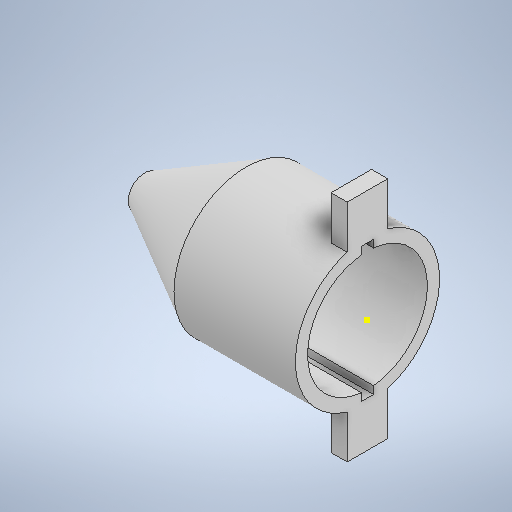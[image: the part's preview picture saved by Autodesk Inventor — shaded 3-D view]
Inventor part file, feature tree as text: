
AUTODESK INVENTOR PART (.ipt)
format: ipt  version: 2025.2 (Build 292293000, 293)  size: 317,952 bytes
history: native  units: in
note: dims shown in document units (in); Inventor stores cm internally (conversion verified against a paired STEP export)
features: sketch x19, extrude x10, revolve x1
ambient origin geometry x8: Origin, YZ Plane, XZ Plane, XY Plane, X Axis, Y Axis, Z Axis, Center Point
bodies: Solid1 (feature_tree)
feature tree (30):
  revolve  "Revolution1"  Angle=90.0deg
  sketch  "Sketch2"  dims[d2=0.3937in d3=0.0in d6=0.5906in d7=0.0in]
  sketch  "Sketch3"  dims[d8=0.1772in d9=0.0787in]
  sketch  "Sketch4"  dims[d10=0.1181in d11=0.0in d12=0.5906in]
  sketch  "Sketch5"  dims[d13=0.0787in d14=0.0591in]
  extrude  "Extrusion1"  Depth=0.5906in TaperAngle=0.0deg
  sketch  "Sketch6"  dims[d15=0.3937in d16=0.0in d17=0.3937in d18=0.0in]
  extrude  "Extrusion2"  Depth=0.0787in
  extrude  "Extrusion3"  Depth=0.5906in
  sketch  "Sketch9"  dims[d25=0.5906in d26=0.0in d29=0.1969in]
  sketch  "Sketch10"  dims[d30=0.0984in d31=0.0787in d32=0.0in]
  sketch  "Sketch11"  dims[d33=0.0354in d34=0.0295in]
  sketch  "Sketch12"  dims[d35=0.3937in d36=0.0in]
  sketch  "Sketch13"  dims[d37=0.1181in]
  extrude  "Extrusion4"  Depth=0.0591in
  extrude  "Extrusion5"  Depth=0.3937in TaperAngle=0.0deg
  extrude  "Extrusion6"  Depth=0.3937in TaperAngle=0.0deg
  extrude  "Extrusion7"  Depth=0.0591in
  extrude  "Extrusion8"  Depth=0.1969in
  sketch  "Sketch16"
  extrude  "Extrusion9"  Depth=0.0787in TaperAngle=0.0deg
  extrude  "Extrusion10"  Depth=0.0295in
  sketch  "Sketch19"
  sketch  "Sketch1"  dims[d0=0.0787in d1=90.0deg]
  sketch  "Sketch7"  dims[d19=0.3937in d20=0.0in d21=0.3937in d22=0.0in]
  sketch  "Sketch8"  dims[d23=0.0591in d24=0.0591in]
  sketch  "Sketch14"
  sketch  "Sketch15"
  sketch  "Sketch17"
  sketch  "Sketch18"
